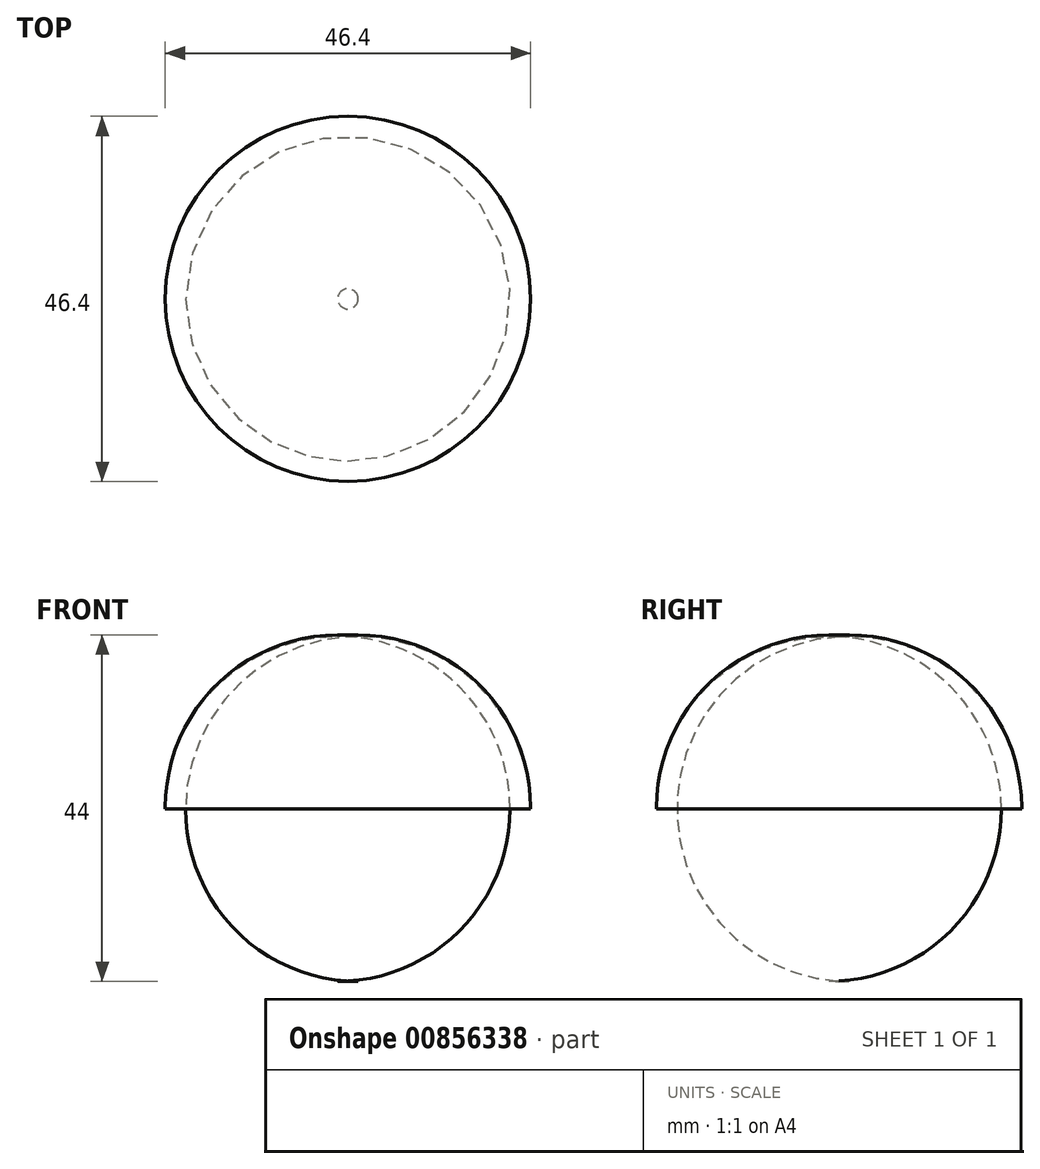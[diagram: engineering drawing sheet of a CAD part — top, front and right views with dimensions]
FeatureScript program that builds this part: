
annotation { "Feature Type Name" : "Feature", "Feature Type Description" : "" }
export const myFeature = defineFeature(function(context is Context, id is Id, definition is map)
    precondition{}
    {
        {
            var Q0;
            Q0=qCreatedBy(makeId("Top.planeOp"),FACE);
            var sketch = newSketch(context, id + "F0", { "sketchPlane" : qUnion([Q0])});
            skCircle(sketch, "E0", {"center": v(0, 0) * mm, "radius": 23.2 * mm});
            skSolve(sketch);
        }
        {
            var Q0;
            Q0=makeQuery(id+"F0.imprint","IMPRINT",FACE,{"disambiguationData":[TD([[makeQuery(id+"F0.imprint","IMPRINT",EDGE,{"derivedFrom":sQuery(id+"F0.wireOp",EDGE,"E0")}),1.0]])]});
            extrude(context, id + "F1", {"entities" : qUnion([Q0]), "depth" : 22 * mm, "offsetDistance" : 25.4 * mm});
        }
        {
            var Q0;
            Q0=makeQuery(id+"F1.opExtrude","CAP_EDGE",EDGE,{"disambiguationData":[OSD([sQuery(id+"F0.wireOp",EDGE,"E0")])],"isStart":false});
            fillet(context, id + "F2", {"entities" : qUnion([Q0]), "radius" : 21.9 * mm, "tangentPropagation" : true, "allowEdgeOverflow" : false});
        }
        {
            var Q0;
            Q0=makeQuery(id+"F1.opExtrude","CAP_FACE",FACE,{"disambiguationData":[OSD([sQuery(id+"F0.wireOp",EDGE,"E0")])],"isStart":true});
            extrude(context, id + "F3", {"entities" : qUnion([Q0]), "operationType" : NewBodyOperationType.ADD, "depth" : 22 * mm, "offsetDistance" : 25.4 * mm});
        }
        {
            var Q0;
            Q0=makeQuery(id+"F3.opExtrude","CAP_EDGE",EDGE,{"disambiguationData":[OSD([sQuery(id+"F0.wireOp",EDGE,"E0")])],"isStart":false});
            fillet(context, id + "F4", {"entities" : qUnion([Q0]), "radius" : 21.9 * mm, "tangentPropagation" : true, "allowEdgeOverflow" : false});
        }
    });
